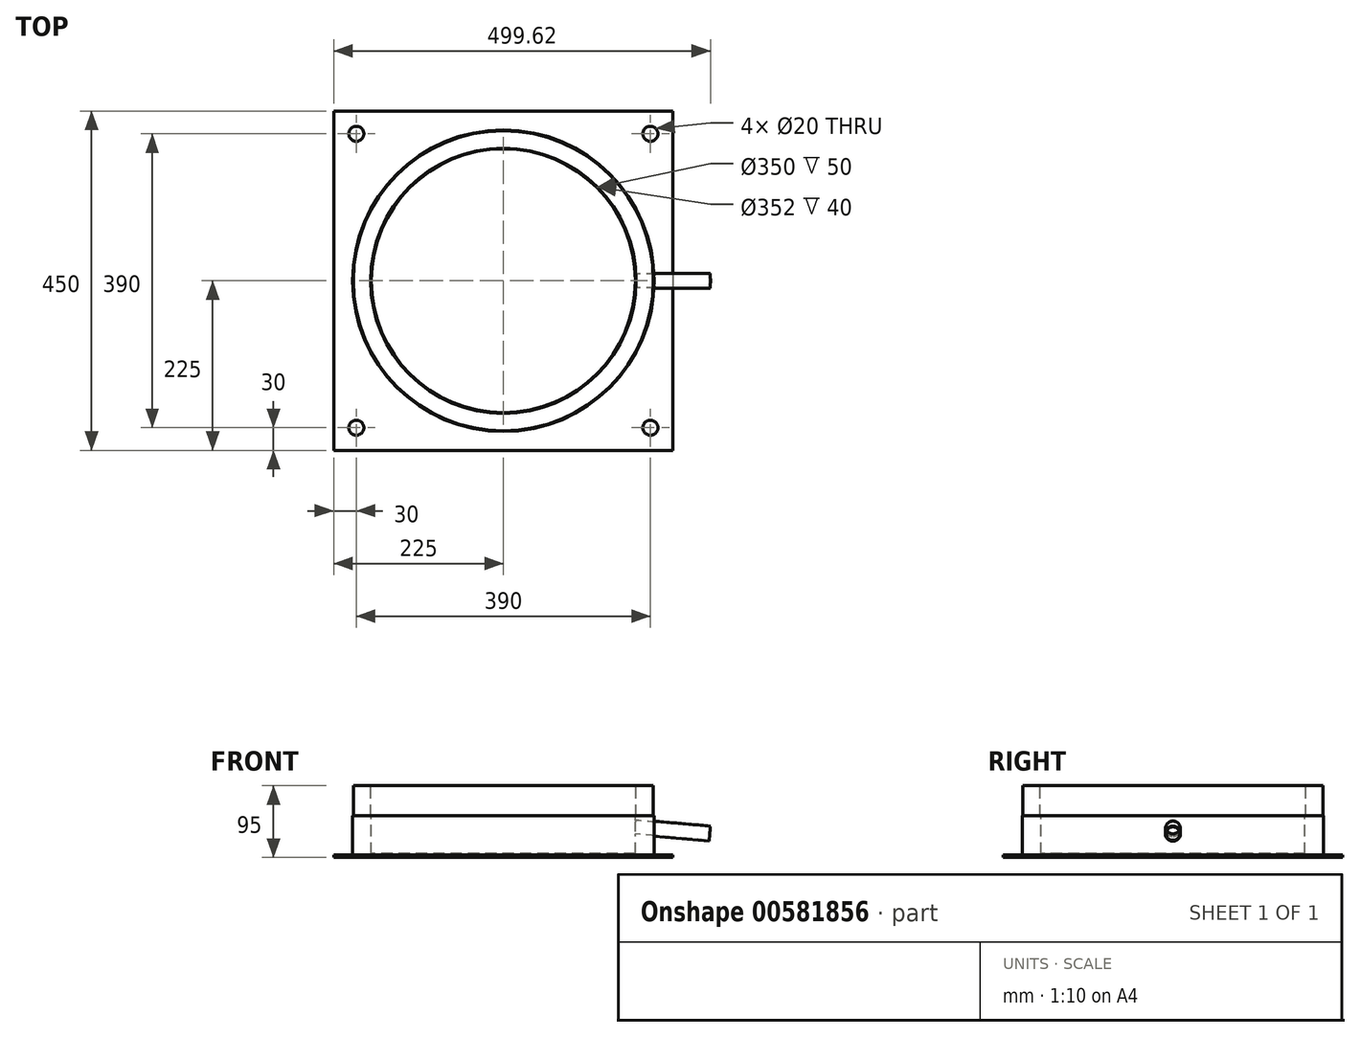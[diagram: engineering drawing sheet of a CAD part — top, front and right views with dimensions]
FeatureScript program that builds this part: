
annotation { "Feature Type Name" : "Feature", "Feature Type Description" : "" }
export const myFeature = defineFeature(function(context is Context, id is Id, definition is map)
    precondition{}
    {
        {
            var Q0;
            Q0=qCreatedBy(makeId("Front.planeOp"),FACE);
            var sketch = newSketch(context, id + "F0", { "sketchPlane" : qUnion([Q0])});
            skLineSegment(sketch, "E0", {"start": v(0, 74.87) * mm, "end": v(0, -73.71) * mm, "construction": true});
            skLineSegment(sketch, "E1", {"start": v(0, 374.84) * mm, "end": v(0, 1) * mm, "construction": true});
            skLineSegment(sketch, "E2", {"start": v(-175, 5) * mm, "end": v(-175, 55) * mm});
            skLineSegment(sketch, "E3", {"start": v(-175, 55) * mm, "end": v(-176, 55) * mm});
            skLineSegment(sketch, "E4", {"start": v(-176, 55) * mm, "end": v(-176, 95) * mm});
            skLineSegment(sketch, "E5", {"start": v(-176, 95) * mm, "end": v(-199, 95) * mm});
            skLineSegment(sketch, "E6", {"start": v(-199, 95) * mm, "end": v(-199, 55) * mm});
            skLineSegment(sketch, "E7", {"start": v(-199, 55) * mm, "end": v(-200, 55) * mm});
            skLineSegment(sketch, "E8", {"start": v(-200, 55) * mm, "end": v(-200, 5) * mm});
            skLineSegment(sketch, "E9", {"start": v(-200, 5) * mm, "end": v(-175, 5) * mm});
            skLineSegment(sketch, "E10.trimOffspring", {"start": v(0, 0) * mm, "end": v(0, -528.94) * mm, "construction": true});
            skLineSegment(sketch, "E11.bottom", {"start": v(-200, 5) * mm, "end": v(-10, 5) * mm});
            skLineSegment(sketch, "E11.top", {"start": v(-200, 2) * mm, "end": v(-10, 2) * mm});
            skLineSegment(sketch, "E11.left", {"start": v(-200, 5) * mm, "end": v(-200, 2) * mm});
            skLineSegment(sketch, "E11.right", {"start": v(-10, 5) * mm, "end": v(-10, 2) * mm});
            skLineSegment(sketch, "E12.bottom", {"start": v(-10, 5) * mm, "end": v(0, 5) * mm});
            skLineSegment(sketch, "E12.top", {"start": v(-10, 2) * mm, "end": v(0, 2) * mm});
            skLineSegment(sketch, "E12.right", {"start": v(0, 5) * mm, "end": v(0, 2) * mm});
            skSolve(sketch);
        }
        {
            var Q0;
            Q0=qSketchRegion(id+"F0",true);
            var Q1;
            Q1=sQuery(id+"F0.wireOp",EDGE,"E1");
            revolve(context, id + "F1", {"entities" : qUnion([Q0]), "axis" : qUnion([Q1]), "revolveType" : RevolveType.FULL});
        }
        {
            var Q0;
            Q0=qCreatedBy(makeId("Top.planeOp"),FACE);
            var sketch = newSketch(context, id + "F2", { "sketchPlane" : qUnion([Q0])});
            skLineSegment(sketch, "E13.bottom", {"start": v(225, 225) * mm, "end": v(-225, 225) * mm});
            skLineSegment(sketch, "E13.top", {"start": v(225, -225) * mm, "end": v(-225, -225) * mm});
            skLineSegment(sketch, "E13.left", {"start": v(225, 225) * mm, "end": v(225, -225) * mm});
            skLineSegment(sketch, "E13.right", {"start": v(-225, 225) * mm, "end": v(-225, -225) * mm});
            skPoint(sketch, "E13.middle", {"position": v(0, 0) * mm});
            skLineSegment(sketch, "E14", {"start": v(0, 0) * mm, "end": v(0, 773.78) * mm, "construction": true});
            skLineSegment(sketch, "E15", {"start": v(0, 0) * mm, "end": v(1007.48, 0) * mm, "construction": true});
            skCircle(sketch, "E16", {"center": v(195, 195) * mm, "radius": 10 * mm});
            skCircle(sketch, "E17.MirrorC", {"center": v(-195, 195) * mm, "radius": 10 * mm});
            skCircle(sketch, "E18.MirrorC", {"center": v(195, -195) * mm, "radius": 10 * mm});
            skCircle(sketch, "E19.MirrorC", {"center": v(-195, -195) * mm, "radius": 10 * mm});
            skSolve(sketch);
        }
        {
            var Q0;
            Q0=qSketchRegion(id+"F2",true);
            extrude(context, id + "F3", {"entities" : qUnion([Q0]), "operationType" : NewBodyOperationType.ADD, "depth" : 3 * mm, "offsetDistance" : 25 * mm});
        }
        {
            var Q0;
            Q0=qCreatedBy(makeId("Front.planeOp"),FACE);
            var sketch = newSketch(context, id + "F4", { "sketchPlane" : qUnion([Q0])});
            skLineSegment(sketch, "E20", {"start": v(200, 38) * mm, "end": v(375.49, 22.65) * mm, "construction": true});
            skLineSegment(sketch, "E21", {"start": v(200, 55) * mm, "end": v(200, 3) * mm, "construction": true});
            skLineSegment(sketch, "E22", {"start": v(175, 50.23) * mm, "end": v(274.62, 41.5) * mm});
            skLineSegment(sketch, "E23", {"start": v(175, 50.23) * mm, "end": v(174.91, 49.23) * mm});
            skLineSegment(sketch, "E24", {"start": v(174.91, 49.23) * mm, "end": v(274.53, 40.51) * mm});
            skLineSegment(sketch, "E25", {"start": v(274.53, 40.51) * mm, "end": v(274.62, 41.5) * mm});
            skSolve(sketch);
        }
        {
            var Q0;
            Q0=qSketchRegion(id+"F4",true);
            var Q1;
            Q1=sQuery(id+"F4.wireOp",EDGE,"E20");
            revolve(context, id + "F5", {"operationType" : NewBodyOperationType.ADD, "surfaceOperationType" : NewSurfaceOperationType.NEW, "entities" : qUnion([Q0]), "axis" : qUnion([Q1]), "revolveType" : RevolveType.FULL});
        }
        {
            var Q0;
            Q0=makeQuery(id+"F5.opRevolve","SWEPT_FACE",FACE,{"disambiguationData":[OSD([sQuery(id+"F4.wireOp",EDGE,"E25")])]});
            var sketch = newSketch(context, id + "F6", { "sketchPlane" : qUnion([Q0])});
            skCircle(sketch, "E26.0", {"center": v(0, 55.29) * mm, "radius": 9 * mm});
            skSolve(sketch);
        }
        {
            var Q0;
            Q0=qSketchRegion(id+"F6",true);
            extrude(context, id + "F7", {"entities" : qUnion([Q0]), "operationType" : NewBodyOperationType.REMOVE, "oppositeDirection" : true, "depth" : 120 * mm, "offsetDistance" : 25 * mm});
        }
        {
            var Q0;
            Q0=makeQuery(id+"F1.opRevolve","SWEPT_FACE",FACE,{"disambiguationData":[OSD([sQuery(id+"F0.wireOp",EDGE,"E11.bottom"),sQuery(id+"F0.wireOp",EDGE,"E12.bottom")])]});
            var sketch = newSketch(context, id + "F8", { "sketchPlane" : qUnion([Q0])});
            skCircle(sketch, "E27.0", {"center": v(0, 0) * mm, "radius": 175 * mm});
            skSolve(sketch);
        }
        {
            var Q0;
            Q0=qSketchRegion(id+"F8",true);
            extrude(context, id + "F9", {"entities" : qUnion([Q0]), "operationType" : NewBodyOperationType.REMOVE, "depth" : 200 * mm, "offsetDistance" : 25 * mm});
        }
    });
